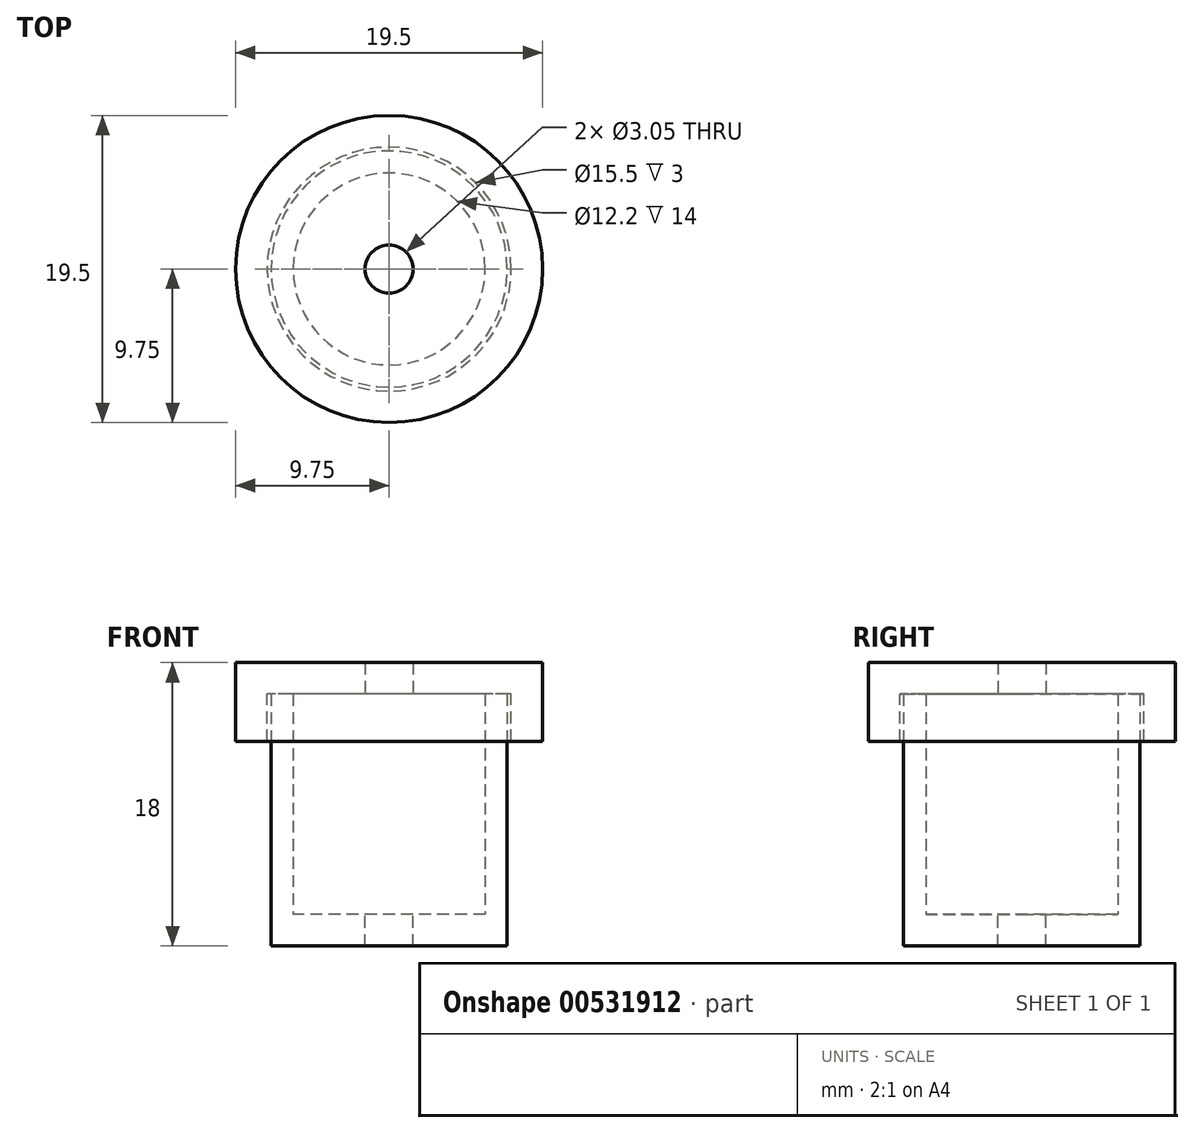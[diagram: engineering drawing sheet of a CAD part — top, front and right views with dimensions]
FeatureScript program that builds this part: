
annotation { "Feature Type Name" : "Feature", "Feature Type Description" : "" }
export const myFeature = defineFeature(function(context is Context, id is Id, definition is map)
    precondition{}
    {
        {
            var Q0;
            Q0=qCreatedBy(makeId("Top.planeOp"),FACE);
            var sketch = newSketch(context, id + "F0", { "sketchPlane" : qUnion([Q0])});
            skCircle(sketch, "E0", {"center": v(0, 0) * mm, "radius": 6.1 * mm});
            skCircle(sketch, "E1", {"center": v(0, 0) * mm, "radius": 7.5 * mm});
            skCircle(sketch, "E2", {"center": v(0, 0) * mm, "radius": 1.52 * mm});
            skSolve(sketch);
        }
        {
            var Q0;
            Q0 = qSketchRegion(id + "F0", true);
            extrude(context, id + "F1", {"entities" : qUnion([Q0]), "depth" : 14 * mm, "offsetDistance" : 25 * mm});
        }
        {
            var Q0;
            Q0=makeQuery(id+"F0.imprint","IMPRINT",FACE,{"disambiguationData":[TD([[makeQuery(id+"F0.imprint","IMPRINT",EDGE,{"derivedFrom":sQuery(id+"F0.wireOp",EDGE,"E0")}),1.0]])]});
            var Q1;
            Q1=makeQuery(id+"F0.imprint","IMPRINT",FACE,{"disambiguationData":[TD([[makeQuery(id+"F0.imprint","IMPRINT",EDGE,{"derivedFrom":sQuery(id+"F0.wireOp",EDGE,"E0")}),-1.0]])]});
            extrude(context, id + "F2", {"entities" : qUnion([Q0, Q1]), "operationType" : NewBodyOperationType.ADD, "oppositeDirection" : true, "depth" : 2 * mm, "offsetDistance" : 25 * mm});
        }
        {
            var Q0;
            Q0=makeQuery(id+"F1.opExtrude","CAP_FACE",FACE,{"disambiguationData":[OSD([sQuery(id+"F0.wireOp",EDGE,"E0"),sQuery(id+"F0.wireOp",EDGE,"E1")])],"isStart":false});
            var sketch = newSketch(context, id + "F3", { "sketchPlane" : qUnion([Q0])});
            skCircle(sketch, "E3.0", {"center": v(0, 0) * mm, "radius": 1.52 * mm});
            skCircle(sketch, "E4", {"center": v(0, 0) * mm, "radius": 7.75 * mm});
            skCircle(sketch, "E5", {"center": v(0, 0) * mm, "radius": 9.75 * mm});
            skSolve(sketch);
        }
        {
            var Q0;
            Q0=makeQuery(id+"F3.imprint","IMPRINT",FACE,{"disambiguationData":[TD([[makeQuery(id+"F3.imprint","IMPRINT",EDGE,{"derivedFrom":sQuery(id+"F3.wireOp",EDGE,"E3.0")}),-1.0]])]});
            var Q1;
            Q1=makeQuery(id+"F3.imprint","IMPRINT",FACE,{"disambiguationData":[TD([[makeQuery(id+"F3.imprint","IMPRINT",EDGE,{"derivedFrom":makeQuery(id+"F1.opExtrude","CAP_EDGE",EDGE,{"disambiguationData":[OSD([sQuery(id+"F0.wireOp",EDGE,"E0")])],"isStart":false})}),-1.0]])]});
            var Q2;
            Q2=makeQuery(id+"F3.imprint","IMPRINT",FACE,{"disambiguationData":[TD([[makeQuery(id+"F3.imprint","IMPRINT",EDGE,{"derivedFrom":sQuery(id+"F3.wireOp",EDGE,"E4")}),1.0]])]});
            var Q3;
            Q3=makeQuery(id+"F3.imprint","IMPRINT",FACE,{"disambiguationData":[TD([[makeQuery(id+"F3.imprint","IMPRINT",EDGE,{"derivedFrom":sQuery(id+"F3.wireOp",EDGE,"E4")}),-1.0]])]});
            extrude(context, id + "F4", {"entities" : qUnion([Q0, Q1, Q2, Q3]), "depth" : 2 * mm, "offsetDistance" : 25 * mm});
        }
        {
            var Q0;
            Q0=makeQuery(id+"F3.imprint","IMPRINT",FACE,{"disambiguationData":[TD([[makeQuery(id+"F3.imprint","IMPRINT",EDGE,{"derivedFrom":sQuery(id+"F3.wireOp",EDGE,"E4")}),-1.0]])]});
            extrude(context, id + "F5", {"entities" : qUnion([Q0]), "operationType" : NewBodyOperationType.ADD, "oppositeDirection" : true, "depth" : 3 * mm, "offsetDistance" : 25 * mm});
        }
    });
